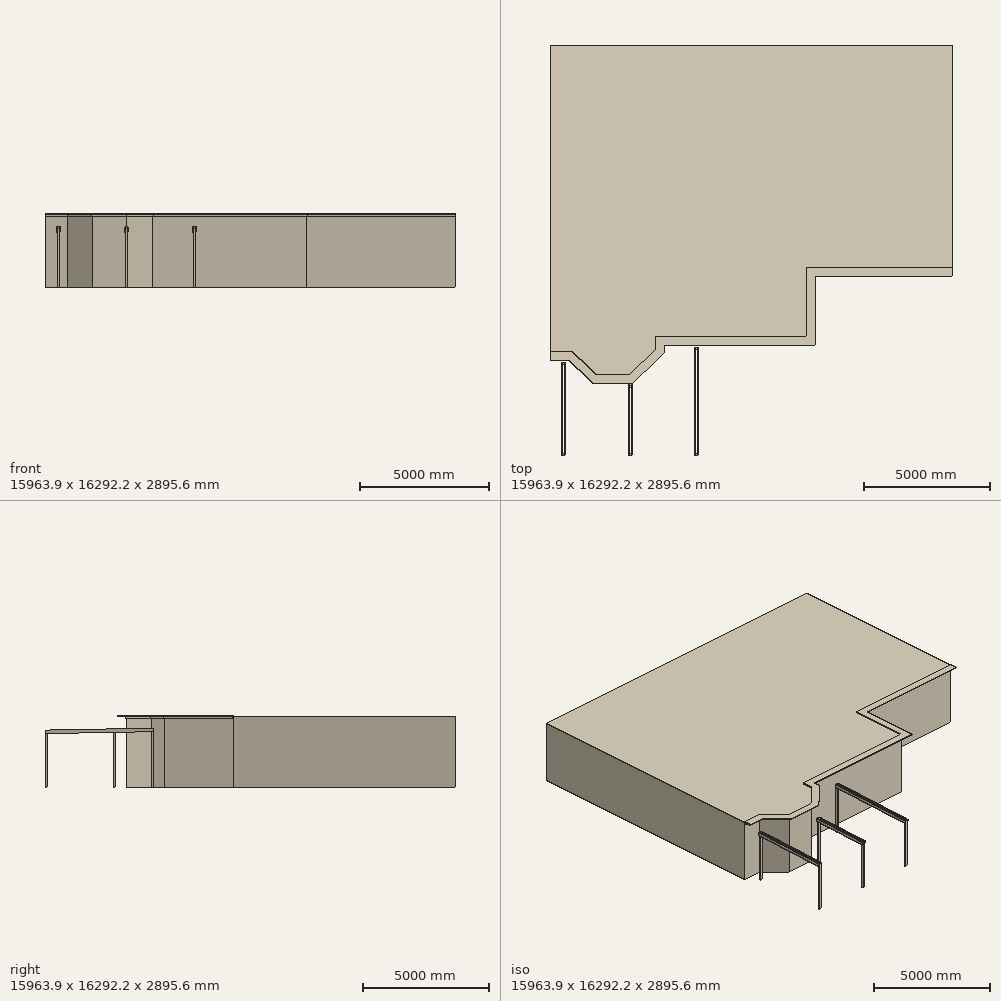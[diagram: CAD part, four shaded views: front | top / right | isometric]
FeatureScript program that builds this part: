
annotation { "Feature Type Name" : "Feature", "Feature Type Description" : "" }
export const myFeature = defineFeature(function(context is Context, id is Id, definition is map)
    precondition{}
    {
        {
            var Q0;
            Q0=qCreatedBy(makeId("Top.planeOp"),FACE);
            var sketch = newSketch(context, id + "F0", { "sketchPlane" : qUnion([Q0])});
            skLineSegment(sketch, "E0", {"start": v(-7981.95, 0) * mm, "end": v(-7981.95, -12171.04) * mm});
            skLineSegment(sketch, "E1", {"start": v(-7981.95, -12171.04) * mm, "end": v(-7118.35, -12171.04) * mm});
            skLineSegment(sketch, "E2", {"start": v(-7118.35, -12171.04) * mm, "end": v(-6165.85, -13072.74) * mm});
            skLineSegment(sketch, "E3", {"start": v(-6165.85, -13072.74) * mm, "end": v(-4832.35, -13072.74) * mm});
            skLineSegment(sketch, "E4", {"start": v(-4832.35, -13072.74) * mm, "end": v(-3803.65, -12090.4) * mm});
            skLineSegment(sketch, "E5", {"start": v(-3803.65, -12090.4) * mm, "end": v(-3803.65, -11582.4) * mm});
            skLineSegment(sketch, "E6", {"start": v(-3803.65, -11582.4) * mm, "end": v(2190.75, -11582.4) * mm});
            skLineSegment(sketch, "E7", {"start": v(2190.75, -11582.4) * mm, "end": v(2190.75, -8839.2) * mm});
            skLineSegment(sketch, "E8", {"start": v(2190.75, -8839.2) * mm, "end": v(7981.95, -8839.2) * mm});
            skLineSegment(sketch, "E9", {"start": v(7981.95, -8839.2) * mm, "end": v(7981.95, 0) * mm});
            skLineSegment(sketch, "E10", {"start": v(7981.95, 0) * mm, "end": v(-7981.95, 0) * mm});
            skSolve(sketch);
        }
        {
            var Q0;
            Q0 = qSketchRegion(id + "F0", true);
            extrude(context, id + "F1", {"entities" : qUnion([Q0]), "depth" : 2857.5 * mm, "offsetDistance" : 25.4 * mm});
        }
        {
            var Q0;
            Q0=makeQuery(id+"F1.opExtrude","CAP_FACE",FACE,{"disambiguationData":[OSD([sQuery(id+"F0.wireOp",EDGE,"E0"),sQuery(id+"F0.wireOp",EDGE,"E1"),sQuery(id+"F0.wireOp",EDGE,"E2"),sQuery(id+"F0.wireOp",EDGE,"E3"),sQuery(id+"F0.wireOp",EDGE,"E4"),sQuery(id+"F0.wireOp",EDGE,"E5"),sQuery(id+"F0.wireOp",EDGE,"E6"),sQuery(id+"F0.wireOp",EDGE,"E7"),sQuery(id+"F0.wireOp",EDGE,"E8"),sQuery(id+"F0.wireOp",EDGE,"E9"),sQuery(id+"F0.wireOp",EDGE,"E10")])],"isStart":false});
            var sketch = newSketch(context, id + "F2", { "sketchPlane" : qUnion([Q0])});
            skLineSegment(sketch, "E11.0", {"start": v(-7981.95, -12171.04) * mm, "end": v(-7118.35, -12171.04) * mm});
            skLineSegment(sketch, "E12.0", {"start": v(-7118.35, -12171.04) * mm, "end": v(-6165.85, -13072.74) * mm});
            skLineSegment(sketch, "E13.0", {"start": v(-6165.85, -13072.74) * mm, "end": v(-4832.35, -13072.74) * mm});
            skLineSegment(sketch, "E14.0", {"start": v(-4832.35, -13072.74) * mm, "end": v(-3803.65, -12090.4) * mm});
            skLineSegment(sketch, "E15.0", {"start": v(-3803.65, -12090.4) * mm, "end": v(-3803.65, -11582.4) * mm});
            skLineSegment(sketch, "E16.0", {"start": v(-3803.65, -11582.4) * mm, "end": v(2190.75, -11582.4) * mm});
            skLineSegment(sketch, "E17.0", {"start": v(2190.75, -11582.4) * mm, "end": v(2190.75, -8839.2) * mm});
            skLineSegment(sketch, "E18.0", {"start": v(2190.75, -8839.2) * mm, "end": v(7981.95, -8839.2) * mm});
            skLineSegment(sketch, "E19.0", {"start": v(2228.85, -8877.3) * mm, "end": v(7981.95, -8877.3) * mm});
            skLineSegment(sketch, "E19.1", {"start": v(2228.85, -11620.5) * mm, "end": v(2228.85, -8877.3) * mm});
            skLineSegment(sketch, "E19.2", {"start": v(-3765.55, -11620.5) * mm, "end": v(2228.85, -11620.5) * mm});
            skLineSegment(sketch, "E19.3", {"start": v(-3765.55, -12106.7) * mm, "end": v(-3765.55, -11620.5) * mm});
            skLineSegment(sketch, "E19.4", {"start": v(-7981.95, -12209.14) * mm, "end": v(-7133.52, -12209.14) * mm});
            skLineSegment(sketch, "E19.5", {"start": v(-7133.52, -12209.14) * mm, "end": v(-6181.02, -13110.84) * mm});
            skLineSegment(sketch, "E19.6", {"start": v(-6181.02, -13110.84) * mm, "end": v(-4817.08, -13110.84) * mm});
            skLineSegment(sketch, "E19.7", {"start": v(-4817.08, -13110.84) * mm, "end": v(-3765.55, -12106.7) * mm});
            skLineSegment(sketch, "E20", {"start": v(-7981.95, -12171.04) * mm, "end": v(-7981.95, -12209.14) * mm});
            skLineSegment(sketch, "E21", {"start": v(7981.95, -8839.2) * mm, "end": v(7981.95, -8877.3) * mm});
            skSolve(sketch);
        }
        {
            var Q0;
            Q0 = qSketchRegion(id + "F2", true);
            extrude(context, id + "F3", {"entities" : qUnion([Q0]), "oppositeDirection" : true, "depth" : 88.9 * mm, "offsetDistance" : 25.4 * mm});
        }
        {
            var Q0;
            Q0=makeQuery(id+"F3.opExtrude","CAP_FACE",FACE,{"disambiguationData":[OSD([sQuery(id+"F2.wireOp",EDGE,"E11.0"),sQuery(id+"F2.wireOp",EDGE,"E12.0"),sQuery(id+"F2.wireOp",EDGE,"E13.0"),sQuery(id+"F2.wireOp",EDGE,"E14.0"),sQuery(id+"F2.wireOp",EDGE,"E15.0"),sQuery(id+"F2.wireOp",EDGE,"E16.0"),sQuery(id+"F2.wireOp",EDGE,"E17.0"),sQuery(id+"F2.wireOp",EDGE,"E18.0"),sQuery(id+"F2.wireOp",EDGE,"E19.0"),sQuery(id+"F2.wireOp",EDGE,"E19.1"),sQuery(id+"F2.wireOp",EDGE,"E19.2"),sQuery(id+"F2.wireOp",EDGE,"E19.3"),sQuery(id+"F2.wireOp",EDGE,"E19.4"),sQuery(id+"F2.wireOp",EDGE,"E19.5"),sQuery(id+"F2.wireOp",EDGE,"E19.6"),sQuery(id+"F2.wireOp",EDGE,"E19.7"),sQuery(id+"F2.wireOp",EDGE,"E20"),sQuery(id+"F2.wireOp",EDGE,"E21")])],"isStart":true});
            var sketch = newSketch(context, id + "F4", { "sketchPlane" : qUnion([Q0])});
            skLineSegment(sketch, "E22.0", {"start": v(-7981.95, -12209.14) * mm, "end": v(-7133.52, -12209.14) * mm});
            skLineSegment(sketch, "E23.0", {"start": v(-7133.52, -12209.14) * mm, "end": v(-6181.02, -13110.84) * mm});
            skLineSegment(sketch, "E24.0", {"start": v(-6181.02, -13110.84) * mm, "end": v(-4817.08, -13110.84) * mm});
            skLineSegment(sketch, "E25.0", {"start": v(-4817.08, -13110.84) * mm, "end": v(-3765.55, -12106.7) * mm});
            skLineSegment(sketch, "E26.0", {"start": v(-3765.55, -12106.7) * mm, "end": v(-3765.55, -11620.5) * mm});
            skLineSegment(sketch, "E27.0", {"start": v(-3765.55, -11620.5) * mm, "end": v(2228.85, -11620.5) * mm});
            skLineSegment(sketch, "E28.0", {"start": v(2228.85, -11620.5) * mm, "end": v(2228.85, -8877.3) * mm});
            skLineSegment(sketch, "E29.0", {"start": v(2228.85, -8877.3) * mm, "end": v(7981.95, -8877.3) * mm});
            skLineSegment(sketch, "E30.0", {"start": v(2533.65, -9182.1) * mm, "end": v(7981.95, -9182.1) * mm});
            skLineSegment(sketch, "E30.1", {"start": v(2533.65, -11925.3) * mm, "end": v(2533.65, -9182.1) * mm});
            skLineSegment(sketch, "E30.2", {"start": v(-3460.75, -11925.3) * mm, "end": v(2533.65, -11925.3) * mm});
            skLineSegment(sketch, "E30.3", {"start": v(-3460.75, -12237.09) * mm, "end": v(-3460.75, -11925.3) * mm});
            skLineSegment(sketch, "E30.4", {"start": v(-7981.95, -12513.94) * mm, "end": v(-7254.91, -12513.94) * mm});
            skLineSegment(sketch, "E30.5", {"start": v(-7254.91, -12513.94) * mm, "end": v(-6302.41, -13415.64) * mm});
            skLineSegment(sketch, "E30.6", {"start": v(-6302.41, -13415.64) * mm, "end": v(-4694.92, -13415.64) * mm});
            skLineSegment(sketch, "E30.7", {"start": v(-4694.92, -13415.64) * mm, "end": v(-3460.75, -12237.09) * mm});
            skLineSegment(sketch, "E31", {"start": v(-7981.95, -12513.94) * mm, "end": v(-7981.95, -12209.14) * mm});
            skLineSegment(sketch, "E32", {"start": v(7981.95, -9182.1) * mm, "end": v(7981.95, -8839.2) * mm});
            skSolve(sketch);
        }
        {
            var Q0;
            Q0 = qSketchRegion(id + "F4", true);
            var Q1;
            Q1=makeQuery(id+"F4.imprint","IMPRINT",FACE,{"disambiguationData":[TD([[makeQuery(id+"F4.imprint","IMPRINT",EDGE,{"derivedFrom":sQuery(id+"F4.wireOp",EDGE,"E22.0")}),1.0]])]});
            extrude(context, id + "F5", {"entities" : qUnion([Q0, Q1]), "depth" : 38.1 * mm, "offsetDistance" : 25.4 * mm});
        }
        {
            var Q0;
            Q0=qCreatedBy(makeId("Top.planeOp"),FACE);
            var sketch = newSketch(context, id + "F6", { "sketchPlane" : qUnion([Q0])});
            skLineSegment(sketch, "E33.bottom", {"start": v(-7524.75, -12602.84) * mm, "end": v(-7435.85, -12602.84) * mm});
            skLineSegment(sketch, "E33.top", {"start": v(-7524.75, -12691.74) * mm, "end": v(-7435.85, -12691.74) * mm});
            skLineSegment(sketch, "E33.left", {"start": v(-7524.75, -12602.84) * mm, "end": v(-7524.75, -12691.74) * mm});
            skLineSegment(sketch, "E33.right", {"start": v(-7435.85, -12602.84) * mm, "end": v(-7435.85, -12691.74) * mm});
            skLineSegment(sketch, "E34.bottom", {"start": v(-4860.02, -13491.84) * mm, "end": v(-4771.12, -13491.84) * mm});
            skLineSegment(sketch, "E34.top", {"start": v(-4860.02, -13580.74) * mm, "end": v(-4771.12, -13580.74) * mm});
            skLineSegment(sketch, "E34.left", {"start": v(-4860.02, -13491.84) * mm, "end": v(-4860.02, -13580.74) * mm});
            skLineSegment(sketch, "E34.right", {"start": v(-4771.12, -13491.84) * mm, "end": v(-4771.12, -13580.74) * mm});
            skLineSegment(sketch, "E35.bottom", {"start": v(-2139.95, -12001.5) * mm, "end": v(-2228.85, -12001.5) * mm});
            skLineSegment(sketch, "E35.top", {"start": v(-2139.95, -12090.4) * mm, "end": v(-2228.85, -12090.4) * mm});
            skLineSegment(sketch, "E35.left", {"start": v(-2139.95, -12001.5) * mm, "end": v(-2139.95, -12090.4) * mm});
            skLineSegment(sketch, "E35.right", {"start": v(-2228.85, -12001.5) * mm, "end": v(-2228.85, -12090.4) * mm});
            skLineSegment(sketch, "E36.bottom", {"start": v(-2228.85, -16203.3) * mm, "end": v(-2139.95, -16203.3) * mm});
            skLineSegment(sketch, "E36.top", {"start": v(-2228.85, -16292.2) * mm, "end": v(-2139.95, -16292.2) * mm});
            skLineSegment(sketch, "E36.left", {"start": v(-2228.85, -16203.3) * mm, "end": v(-2228.85, -16292.2) * mm});
            skLineSegment(sketch, "E36.right", {"start": v(-2139.95, -16203.3) * mm, "end": v(-2139.95, -16292.2) * mm});
            skLineSegment(sketch, "E37.bottom", {"start": v(-4860.02, -16203.3) * mm, "end": v(-4771.12, -16203.3) * mm});
            skLineSegment(sketch, "E37.top", {"start": v(-4860.02, -16292.2) * mm, "end": v(-4771.12, -16292.2) * mm});
            skLineSegment(sketch, "E37.left", {"start": v(-4860.02, -16203.3) * mm, "end": v(-4860.02, -16292.2) * mm});
            skLineSegment(sketch, "E37.right", {"start": v(-4771.12, -16203.3) * mm, "end": v(-4771.12, -16292.2) * mm});
            skLineSegment(sketch, "E38.bottom", {"start": v(-7524.75, -16203.3) * mm, "end": v(-7435.85, -16203.3) * mm});
            skLineSegment(sketch, "E38.top", {"start": v(-7524.75, -16292.2) * mm, "end": v(-7435.85, -16292.2) * mm});
            skLineSegment(sketch, "E38.left", {"start": v(-7524.75, -16203.3) * mm, "end": v(-7524.75, -16292.2) * mm});
            skLineSegment(sketch, "E38.right", {"start": v(-7435.85, -16203.3) * mm, "end": v(-7435.85, -16292.2) * mm});
            skSolve(sketch);
        }
        {
            var Q0;
            Q0=makeQuery(id+"F6.imprint","IMPRINT",FACE,{"disambiguationData":[TD([[makeQuery(id+"F6.imprint","IMPRINT",EDGE,{"derivedFrom":sQuery(id+"F6.wireOp",EDGE,"E33.bottom")}),-1.0]])]});
            var Q1;
            Q1=makeQuery(id+"F6.imprint","IMPRINT",FACE,{"disambiguationData":[TD([[makeQuery(id+"F6.imprint","IMPRINT",EDGE,{"derivedFrom":sQuery(id+"F6.wireOp",EDGE,"E34.bottom")}),-1.0]])]});
            var Q2;
            Q2=makeQuery(id+"F6.imprint","IMPRINT",FACE,{"disambiguationData":[TD([[makeQuery(id+"F6.imprint","IMPRINT",EDGE,{"derivedFrom":sQuery(id+"F6.wireOp",EDGE,"E35.bottom")}),1.0]])]});
            extrude(context, id + "F7", {"entities" : qUnion([Q0, Q1, Q2]), "depth" : 2374.9 * mm, "offsetDistance" : 25.4 * mm});
        }
        {
            var Q0;
            Q0=makeQuery(id+"F6.imprint","IMPRINT",FACE,{"disambiguationData":[TD([[makeQuery(id+"F6.imprint","IMPRINT",EDGE,{"derivedFrom":sQuery(id+"F6.wireOp",EDGE,"E38.bottom")}),-1.0]])]});
            var Q1;
            Q1=makeQuery(id+"F6.imprint","IMPRINT",FACE,{"disambiguationData":[TD([[makeQuery(id+"F6.imprint","IMPRINT",EDGE,{"derivedFrom":sQuery(id+"F6.wireOp",EDGE,"E37.bottom")}),-1.0]])]});
            var Q2;
            Q2=makeQuery(id+"F6.imprint","IMPRINT",FACE,{"disambiguationData":[TD([[makeQuery(id+"F6.imprint","IMPRINT",EDGE,{"derivedFrom":sQuery(id+"F6.wireOp",EDGE,"E36.bottom")}),-1.0]])]});
            extrude(context, id + "F8", {"entities" : qUnion([Q0, Q1, Q2]), "depth" : 2298.7 * mm, "offsetDistance" : 25.4 * mm});
        }
        {
            var Q0;
            Q0=makeQuery(id+"F7.opExtrude","CAP_VERTEX",VERTEX,{"disambiguationData":[OSD([sQuery(id+"F6.wireOp",EDGE,"E35.bottom"),sQuery(id+"F6.wireOp",EDGE,"E35.left")])],"isStart":false});
            var Q1;
            Q1=makeQuery(id+"F8.opExtrude","CAP_VERTEX",VERTEX,{"disambiguationData":[OSD([sQuery(id+"F6.wireOp",EDGE,"E36.top"),sQuery(id+"F6.wireOp",EDGE,"E36.right")])],"isStart":false});
            var Q2;
            Q2=makeQuery(id+"F8.opExtrude","CAP_VERTEX",VERTEX,{"disambiguationData":[OSD([sQuery(id+"F6.wireOp",EDGE,"E36.top"),sQuery(id+"F6.wireOp",EDGE,"E36.left")])],"isStart":false});
            cPlane(context, id + "F9", {"entities" : qUnion([Q0, Q1, Q2]), "cplaneType" : CPlaneType.THREE_POINT, "offset" : 25.4 * mm, "width" : 152.4 * mm, "height" : 152.4 * mm});
        }
        {
            var Q0;
            Q0=qCreatedBy(id+"F9.planeOp",FACE);
            var sketch = newSketch(context, id + "F10", { "sketchPlane" : qUnion([Q0])});
            skLineSegment(sketch, "E39.bottom", {"start": v(-2139.95, -16248.8) * mm, "end": v(-2101.85, -16248.8) * mm});
            skLineSegment(sketch, "E39.top", {"start": v(-2139.95, -11957.44) * mm, "end": v(-2101.85, -11957.44) * mm});
            skLineSegment(sketch, "E39.left", {"start": v(-2139.95, -16248.8) * mm, "end": v(-2139.95, -11957.44) * mm});
            skLineSegment(sketch, "E39.right", {"start": v(-2101.85, -16248.8) * mm, "end": v(-2101.85, -11957.44) * mm});
            skLineSegment(sketch, "E40.bottom", {"start": v(-2266.95, -16248.8) * mm, "end": v(-2228.85, -16248.8) * mm});
            skLineSegment(sketch, "E40.top", {"start": v(-2266.95, -11957.44) * mm, "end": v(-2228.85, -11957.44) * mm});
            skLineSegment(sketch, "E40.left", {"start": v(-2266.95, -16248.8) * mm, "end": v(-2266.95, -11957.44) * mm});
            skLineSegment(sketch, "E40.right", {"start": v(-2228.85, -16248.8) * mm, "end": v(-2228.85, -11957.44) * mm});
            skLineSegment(sketch, "E41.bottom", {"start": v(-4771.12, -16248.8) * mm, "end": v(-4733.02, -16248.8) * mm});
            skLineSegment(sketch, "E41.top", {"start": v(-4771.12, -13448.02) * mm, "end": v(-4733.02, -13448.02) * mm});
            skLineSegment(sketch, "E41.left", {"start": v(-4771.12, -16248.8) * mm, "end": v(-4771.12, -13448.02) * mm});
            skLineSegment(sketch, "E41.right", {"start": v(-4733.02, -16248.8) * mm, "end": v(-4733.02, -13448.02) * mm});
            skLineSegment(sketch, "E42.bottom", {"start": v(-4898.12, -16248.8) * mm, "end": v(-4860.02, -16248.8) * mm});
            skLineSegment(sketch, "E42.top", {"start": v(-4898.12, -13448.02) * mm, "end": v(-4860.02, -13448.02) * mm});
            skLineSegment(sketch, "E42.left", {"start": v(-4898.12, -16248.8) * mm, "end": v(-4898.12, -13448.02) * mm});
            skLineSegment(sketch, "E42.right", {"start": v(-4860.02, -16248.8) * mm, "end": v(-4860.02, -13448.02) * mm});
            skLineSegment(sketch, "E43.bottom", {"start": v(-7397.75, -16248.8) * mm, "end": v(-7435.85, -16248.8) * mm});
            skLineSegment(sketch, "E43.top", {"start": v(-7397.75, -12558.88) * mm, "end": v(-7435.85, -12558.88) * mm});
            skLineSegment(sketch, "E43.left", {"start": v(-7397.75, -16248.8) * mm, "end": v(-7397.75, -12558.88) * mm});
            skLineSegment(sketch, "E43.right", {"start": v(-7435.85, -16248.8) * mm, "end": v(-7435.85, -12558.88) * mm});
            skLineSegment(sketch, "E44.bottom", {"start": v(-7524.75, -16248.8) * mm, "end": v(-7562.85, -16248.8) * mm});
            skLineSegment(sketch, "E44.top", {"start": v(-7524.75, -12558.88) * mm, "end": v(-7562.85, -12558.88) * mm});
            skLineSegment(sketch, "E44.left", {"start": v(-7524.75, -16248.8) * mm, "end": v(-7524.75, -12558.88) * mm});
            skLineSegment(sketch, "E44.right", {"start": v(-7562.85, -16248.8) * mm, "end": v(-7562.85, -12558.88) * mm});
            skSolve(sketch);
        }
        {
            var Q0;
            Q0 = qSketchRegion(id + "F10", true);
            extrude(context, id + "F11", {"entities" : qUnion([Q0]), "oppositeDirection" : true, "depth" : 139.7 * mm, "offsetDistance" : 25.4 * mm});
        }
    });
